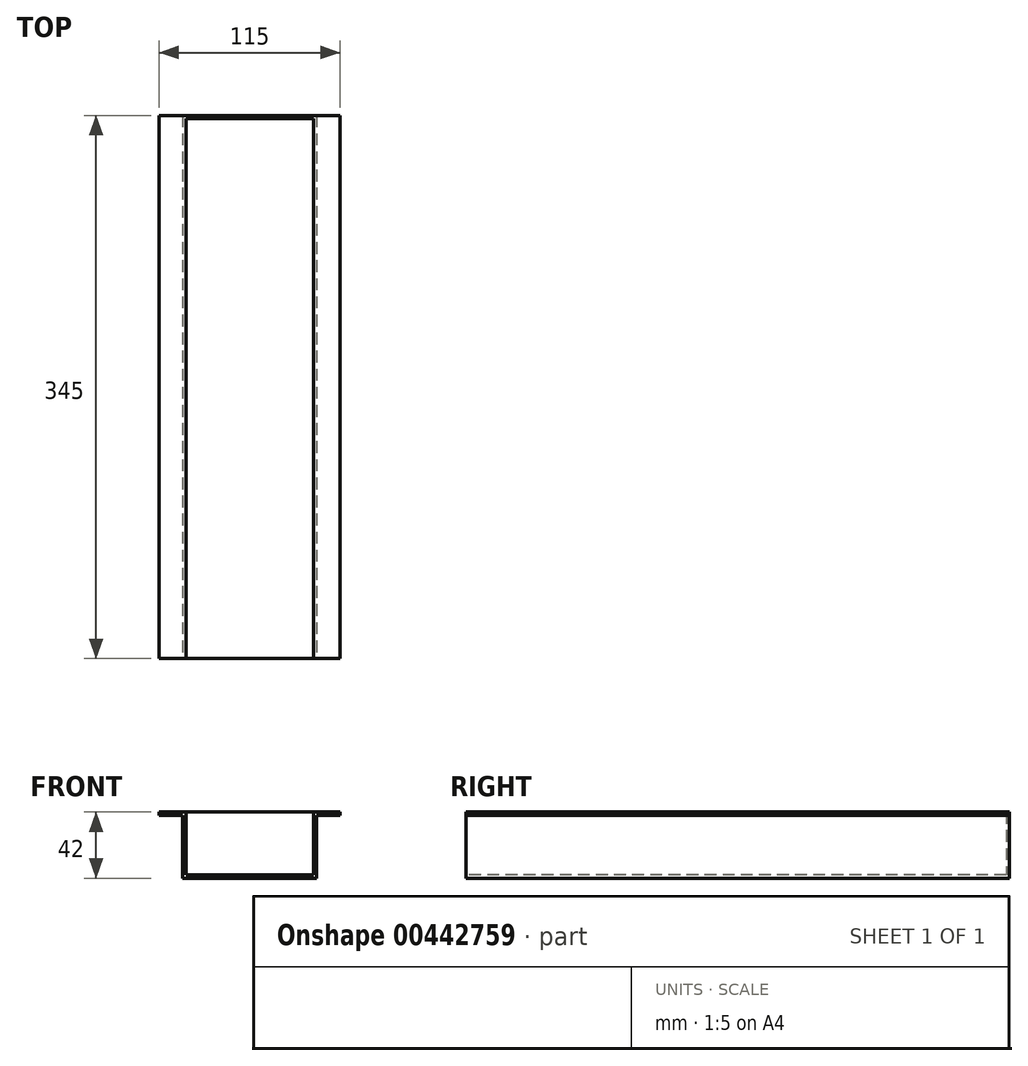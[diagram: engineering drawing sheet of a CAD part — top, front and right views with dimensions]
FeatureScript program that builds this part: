
annotation { "Feature Type Name" : "Feature", "Feature Type Description" : "" }
export const myFeature = defineFeature(function(context is Context, id is Id, definition is map)
    precondition{}
    {
        {
            var Q0;
            Q0=qCreatedBy(makeId("Top.planeOp"),FACE);
            var sketch = newSketch(context, id + "F0", { "sketchPlane" : qUnion([Q0])});
            skLineSegment(sketch, "E0.bottom", {"start": v(42.5, 172.5) * mm, "end": v(-42.5, 172.5) * mm});
            skLineSegment(sketch, "E0.top", {"start": v(42.5, -172.5) * mm, "end": v(-42.5, -172.5) * mm});
            skLineSegment(sketch, "E0.left", {"start": v(42.5, 172.5) * mm, "end": v(42.5, -172.5) * mm});
            skLineSegment(sketch, "E0.right", {"start": v(-42.5, 172.5) * mm, "end": v(-42.5, -172.5) * mm});
            skPoint(sketch, "E0.middle", {"position": v(0, 0) * mm});
            skSolve(sketch);
        }
        {
            var Q0;
            Q0 = qSketchRegion(id + "F0", true);
            extrude(context, id + "F1", {"entities" : qUnion([Q0]), "depth" : 42 * mm});
        }
        {
            var Q0;
            Q0=makeQuery(id+"F1.opExtrude","CAP_FACE",FACE,{"disambiguationData":[OSD([sQuery(id+"F0.wireOp",EDGE,"E0.bottom"),sQuery(id+"F0.wireOp",EDGE,"E0.top"),sQuery(id+"F0.wireOp",EDGE,"E0.left"),sQuery(id+"F0.wireOp",EDGE,"E0.right")])],"isStart":false});
            shell(context, id + "F2", {"entities" : qUnion([Q0]), "thickness" : 2 * mm});
        }
        {
            var Q0;
            Q0=qCreatedBy(makeId("Front.planeOp"),FACE);
            var sketch = newSketch(context, id + "F3", { "sketchPlane" : qUnion([Q0])});
            skLineSegment(sketch, "E1.0", {"start": v(-40.5, 42) * mm, "end": v(-40.5, 2) * mm});
            skLineSegment(sketch, "E2.0", {"start": v(40.5, 2) * mm, "end": v(-40.5, 2) * mm});
            skLineSegment(sketch, "E3.0", {"start": v(40.5, 42) * mm, "end": v(40.5, 2) * mm});
            skLineSegment(sketch, "E4.0", {"start": v(40.5, 42) * mm, "end": v(-40.5, 42) * mm});
            skSolve(sketch);
        }
        {
            var Q0;
            Q0 = qSketchRegion(id + "F3", true);
            var Q1;
            Q1=makeQuery(id+"F1.opExtrude","SWEPT_FACE",FACE,{"disambiguationData":[OSD([sQuery(id+"F0.wireOp",EDGE,"E0.top")])]});
            var Q2;
            Q2=makeQuery(id+"F1.opExtrude","SWEPT_FACE",FACE,{"disambiguationData":[OSD([sQuery(id+"F0.wireOp",EDGE,"E0.bottom")])]});
            extrude(context, id + "F4", {"entities" : qUnion([Q0]), "operationType" : NewBodyOperationType.REMOVE, "endBound" : BoundingType.UP_TO_SURFACE, "endBoundEntityFace" : qUnion([Q1]), "depth" : 25 * mm, "hasSecondDirection" : true, "secondDirectionBound" : SecondDirectionBoundingType.UP_TO_SURFACE, "secondDirectionOppositeDirection" : true, "secondDirectionBoundEntityFace" : qUnion([Q2]), "secondDirectionDepth" : 25 * mm});
        }
        {
            var Q0;
            Q0=qCreatedBy(makeId("Top.planeOp"),FACE);
            var sketch = newSketch(context, id + "F5", { "sketchPlane" : qUnion([Q0])});
            skLineSegment(sketch, "E5", {"start": v(-42.5, -172.5) * mm, "end": v(-57.5, -172.5) * mm});
            skLineSegment(sketch, "E6", {"start": v(-57.5, -172.5) * mm, "end": v(-57.5, 172.5) * mm});
            skLineSegment(sketch, "E7", {"start": v(-57.5, 172.5) * mm, "end": v(-42.5, 172.5) * mm});
            skLineSegment(sketch, "E8.0", {"start": v(-42.5, 172.5) * mm, "end": v(-42.5, -172.5) * mm});
            skLineSegment(sketch, "E9.MirrorCS", {"start": v(57.5, 172.5) * mm, "end": v(42.5, 172.5) * mm});
            skLineSegment(sketch, "E10.MirrorCS", {"start": v(42.5, 172.5) * mm, "end": v(42.5, -172.5) * mm});
            skLineSegment(sketch, "E11.MirrorCS", {"start": v(57.5, -172.5) * mm, "end": v(57.5, 172.5) * mm});
            skLineSegment(sketch, "E12.MirrorCS", {"start": v(42.5, -172.5) * mm, "end": v(57.5, -172.5) * mm});
            skSolve(sketch);
        }
        {
            var Q0;
            Q0 = qSketchRegion(id + "F5", true);
            extrude(context, id + "F6", {"entities" : qUnion([Q0]), "operationType" : NewBodyOperationType.ADD, "depth" : 42 * mm, "hasSecondDirection" : true, "secondDirectionOppositeDirection" : false, "secondDirectionDepth" : 40 * mm});
        }
        {
            var Q0;
            Q0=qCreatedBy(makeId("Front.planeOp"),FACE);
            var sketch = newSketch(context, id + "F7", { "sketchPlane" : qUnion([Q0])});
            skLineSegment(sketch, "E13.0", {"start": v(-40.5, 42) * mm, "end": v(-40.5, 2) * mm});
            skLineSegment(sketch, "E14.0", {"start": v(40.5, 2) * mm, "end": v(-40.5, 2) * mm});
            skLineSegment(sketch, "E15.0", {"start": v(40.5, 42) * mm, "end": v(40.5, 2) * mm});
            skLineSegment(sketch, "E16", {"start": v(40.5, 42) * mm, "end": v(-40.5, 42) * mm});
            skSolve(sketch);
        }
        {
            var Q0;
            Q0 = qSketchRegion(id + "F7", true);
            var Q1;
            Q1=makeQuery(id+"F6.boolean.opBoolean","MERGE",FACE,{"derivedFrom":[makeQuery(id+"F1.opExtrude","SWEPT_FACE",FACE,{"disambiguationData":[OSD([sQuery(id+"F0.wireOp",EDGE,"E0.bottom")])]}),makeQuery(id+"F6.opExtrude","SWEPT_FACE",FACE,{"disambiguationData":[OSD([sQuery(id+"F5.wireOp",EDGE,"E7")])]}),makeQuery(id+"F6.opExtrude","SWEPT_FACE",FACE,{"disambiguationData":[OSD([sQuery(id+"F5.wireOp",EDGE,"E9.MirrorCS")])]})]});
            var Q2;
            Q2=makeQuery(id+"F1.opExtrude","SWEPT_BODY",BODY,{"disambiguationData":[OSD([sQuery(id+"F0.wireOp",EDGE,"E0.bottom"),sQuery(id+"F0.wireOp",EDGE,"E0.top"),sQuery(id+"F0.wireOp",EDGE,"E0.left"),sQuery(id+"F0.wireOp",EDGE,"E0.right")])]});
            extrude(context, id + "F8", {"entities" : qUnion([Q0]), "operationType" : NewBodyOperationType.ADD, "endBound" : BoundingType.UP_TO_SURFACE, "oppositeDirection" : true, "endBoundEntityFace" : qUnion([Q1]), "endBoundEntityBody" : qUnion([Q2]), "depth" : 55 * mm, "hasSecondDirection" : true, "secondDirectionOppositeDirection" : true, "secondDirectionDepth" : 170.5 * mm});
        }
    });
